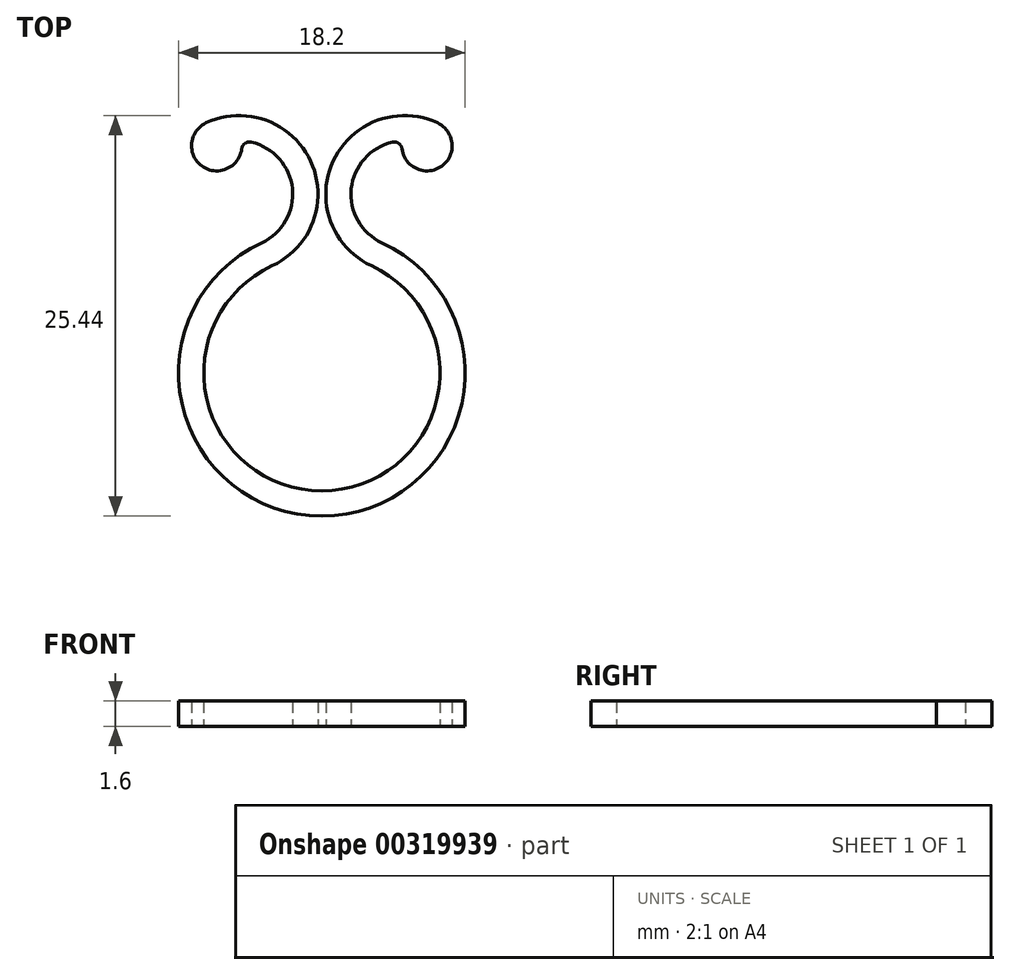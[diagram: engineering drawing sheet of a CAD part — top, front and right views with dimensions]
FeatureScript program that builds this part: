
annotation { "Feature Type Name" : "Feature", "Feature Type Description" : "" }
export const myFeature = defineFeature(function(context is Context, id is Id, definition is map)
    precondition{}
    {
        {
            var Q0;
            Q0=qCreatedBy(makeId("Top.planeOp"),FACE);
            var sketch = newSketch(context, id + "F0", { "sketchPlane" : qUnion([Q0])});
            skCircle(sketch, "E0", {"center": v(0, 0) * mm, "radius": 7.5 * mm, "construction": true});
            skSolve(sketch);
        }
        {
            var Q0;
            Q0=qCreatedBy(makeId("Top.planeOp"),FACE);
            var sketch = newSketch(context, id + "F1", { "sketchPlane" : qUnion([Q0])});
            skArc(sketch, "E1", {"start": v(-3.15, 6.8) * mm, "mid": v(0, -7.5) * mm, "end": v(3.15, 6.8) * mm});
            skArc(sketch, "E2", {"start": v(7.35, 15.88) * mm, "mid": v(0.71, 13.44) * mm, "end": v(3.15, 6.8) * mm});
            skArc(sketch, "E3", {"start": v(-3.15, 6.8) * mm, "mid": v(-0.71, 13.44) * mm, "end": v(-7.35, 15.88) * mm});
            skLineSegment(sketch, "E4", {"start": v(-3.15, 6.8) * mm, "end": v(3.15, 6.8) * mm, "construction": true});
            skLineSegment(sketch, "E5", {"start": v(0, 0) * mm, "end": v(3.15, 6.8) * mm, "construction": true});
            skLineSegment(sketch, "E6", {"start": v(-3.15, 6.8) * mm, "end": v(0, 0) * mm, "construction": true});
            skLineSegment(sketch, "E7", {"start": v(-5.25, 11.34) * mm, "end": v(-0.25, 11.34) * mm, "construction": true});
            skLineSegment(sketch, "E8", {"start": v(-0.25, 11.34) * mm, "end": v(0.25, 11.34) * mm, "construction": true});
            skLineSegment(sketch, "E9", {"start": v(0.25, 11.34) * mm, "end": v(5.25, 11.34) * mm, "construction": true});
            skArc(sketch, "E10.0", {"start": v(-3.82, 8.26) * mm, "mid": v(0, -9.1) * mm, "end": v(3.82, 8.26) * mm});
            skArc(sketch, "E11", {"start": v(5.1, 14.74) * mm, "mid": v(1.92, 12) * mm, "end": v(3.82, 8.26) * mm});
            skArc(sketch, "E12", {"start": v(5.1, 14.74) * mm, "mid": v(7.4, 13) * mm, "end": v(7.35, 15.88) * mm});
            skLineSegment(sketch, "E13", {"start": v(3.15, 6.8) * mm, "end": v(3.82, 8.26) * mm, "construction": true});
            skLineSegment(sketch, "E14", {"start": v(6.68, 14.43) * mm, "end": v(3.82, 8.26) * mm, "construction": true});
            skLineSegment(sketch, "E15", {"start": v(-3.15, 6.8) * mm, "end": v(-3.82, 8.26) * mm, "construction": true});
            skLineSegment(sketch, "E16", {"start": v(-6.68, 14.43) * mm, "end": v(-3.82, 8.26) * mm, "construction": true});
            skLineSegment(sketch, "E17", {"start": v(-6.68, 14.43) * mm, "end": v(-7.35, 15.88) * mm, "construction": true});
            skLineSegment(sketch, "E18", {"start": v(7.35, 15.88) * mm, "end": v(6.68, 14.43) * mm, "construction": true});
            skLineSegment(sketch, "E19", {"start": v(0, 0) * mm, "end": v(0, -7.5) * mm, "construction": true});
            skArc(sketch, "E20.MirrorCS", {"start": v(-5.1, 14.74) * mm, "mid": v(-1.92, 12) * mm, "end": v(-3.82, 8.26) * mm});
            skArc(sketch, "E21.MirrorCS", {"start": v(-5.1, 14.74) * mm, "mid": v(-7.4, 13) * mm, "end": v(-7.35, 15.88) * mm});
            skSolve(sketch);
        }
        {
            var Q0;
            Q0=makeQuery(id+"F1.imprint","IMPRINT",FACE,{"disambiguationData":[TD([[makeQuery(id+"F1.imprint","IMPRINT",EDGE,{"derivedFrom":sQuery(id+"F1.wireOp",EDGE,"E1")}),-1.0]])]});
            extrude(context, id + "F2", {"entities" : qUnion([Q0]), "depth" : 1.6 * mm});
        }
        {
            var Q0;
            Q0=makeQuery(id+"F2.opExtrude","SWEPT_EDGE",EDGE,{"disambiguationData":[OSD([sQuery(id+"F1.wireOp",EDGE,"E11"),sQuery(id+"F1.wireOp",EDGE,"E12")])]});
            var Q1;
            Q1=makeQuery(id+"F2.opExtrude","SWEPT_EDGE",EDGE,{"disambiguationData":[OSD([sQuery(id+"F1.wireOp",EDGE,"E20.MirrorCS"),sQuery(id+"F1.wireOp",EDGE,"E21.MirrorCS")])]});
            fillet(context, id + "F3", {"entities" : qUnion([Q0, Q1]), "radius" : .5 * mm, "tangentPropagation" : true, "allowEdgeOverflow" : false});
        }
    });
